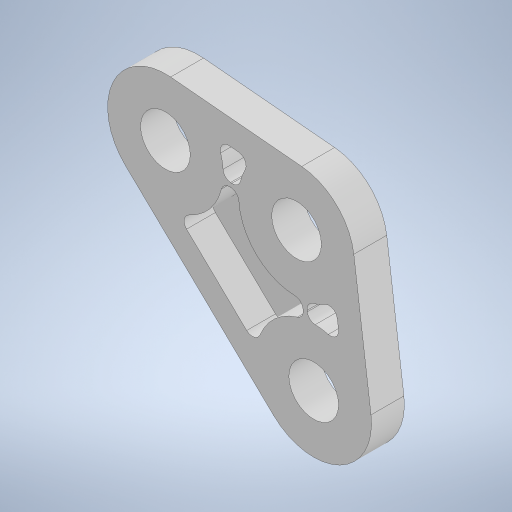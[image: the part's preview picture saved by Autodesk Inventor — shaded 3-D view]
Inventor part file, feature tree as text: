
AUTODESK INVENTOR PART (.ipt)
format: ipt  version: 2023 (Build 270158030, 158C)  size: 349,184 bytes
history: native  units: mm
features: sketch x4, extrude x3, projected_geometry x3, other x1, fillet x1
ambient origin geometry x8: Origin, YZ Plane, XZ Plane, XY Plane, X Axis, Y Axis, Z Axis, Center Point
bodies: Body1 (feature_tree)
feature tree (12):
  other  "ソリッド1"
  extrude  "押し出し1"  Depth=4.0mm TaperAngle=0.0deg
  sketch  "スケッチ2"
  extrude  "押し出し2"  Depth=3.0mm
  extrude  "押し出し3"  Depth=3.5mm TaperAngle=0.0deg
  fillet  "フィレット1"  Radius=0.5mm
  sketch  "スケッチ1"
  projected_geometry  "投影ループ1"
  sketch  "スケッチ3"
  projected_geometry  "投影ループ2"
  sketch  "スケッチ4"
  projected_geometry  "投影ループ3"
